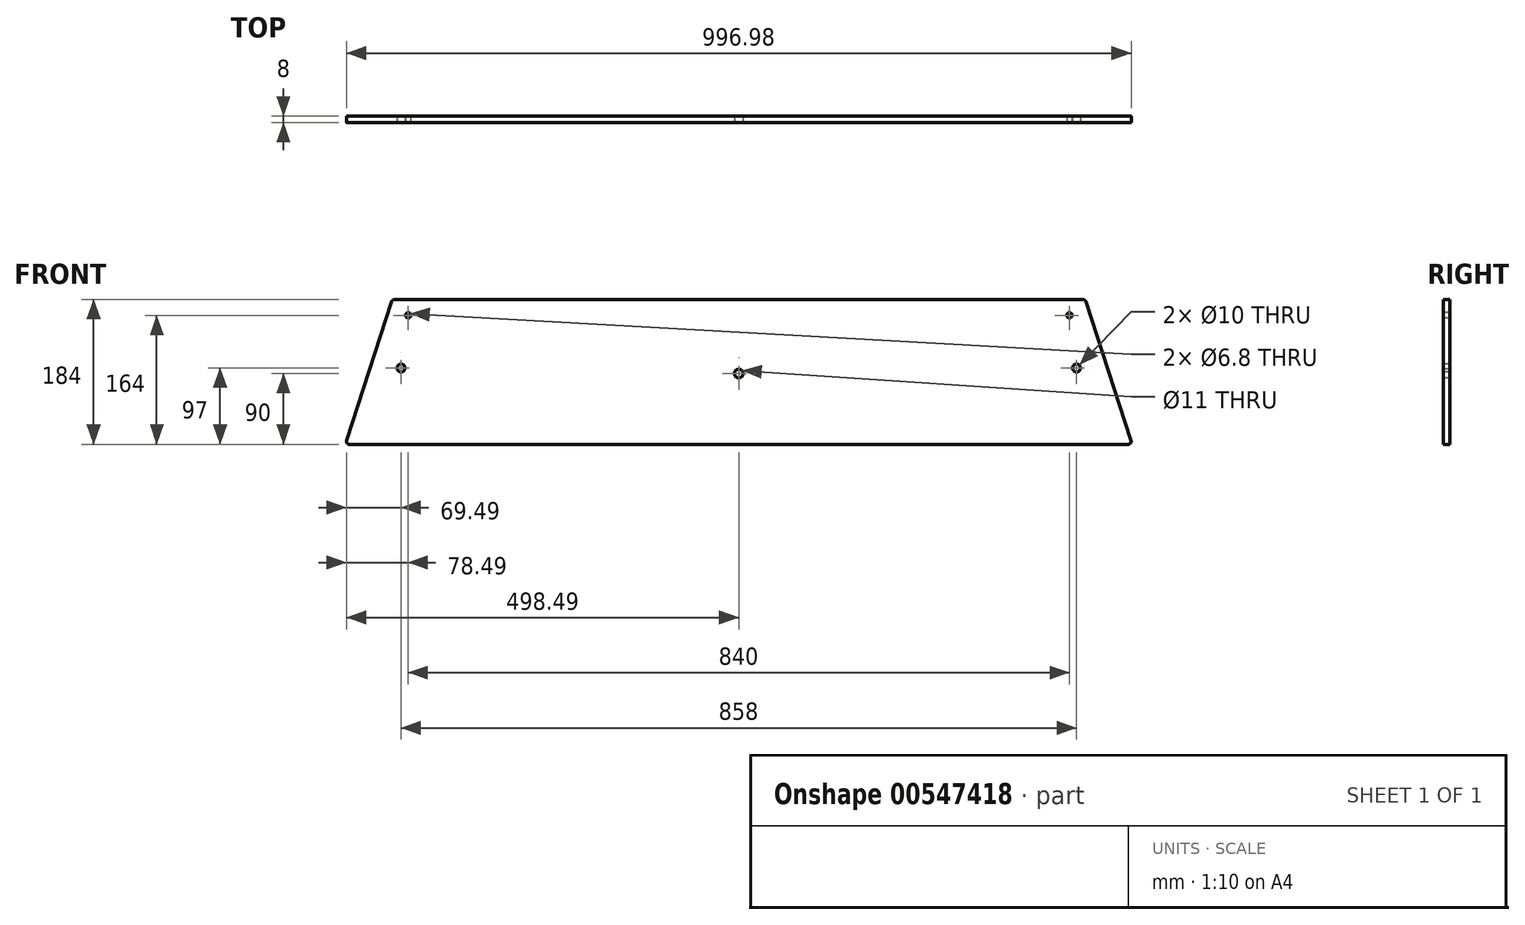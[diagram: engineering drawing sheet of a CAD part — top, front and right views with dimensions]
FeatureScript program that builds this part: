
annotation { "Feature Type Name" : "Feature", "Feature Type Description" : "" }
export const myFeature = defineFeature(function(context is Context, id is Id, definition is map)
    precondition{}
    {
        {
            var Q0;
            Q0=qCreatedBy(makeId("Front.planeOp"),FACE);
            var sketch = newSketch(context, id + "F0", { "sketchPlane" : qUnion([Q0])});
            skLineSegment(sketch, "E0.bottom", {"start": v(440, 92) * mm, "end": v(-440, 92) * mm});
            skLineSegment(sketch, "E0.top", {"start": v(440, -92) * mm, "end": v(-440, -92) * mm});
            skPoint(sketch, "E0.middle", {"position": v(0, 0) * mm});
            skLineSegment(sketch, "E1", {"start": v(440, 92) * mm, "end": v(500, -92) * mm});
            skLineSegment(sketch, "E2", {"start": v(500, -92) * mm, "end": v(440, -92) * mm});
            skLineSegment(sketch, "E3", {"start": v(-440, 92) * mm, "end": v(-500, -92) * mm});
            skLineSegment(sketch, "E4", {"start": v(-500, -92) * mm, "end": v(-440, -92) * mm});
            skSolve(sketch);
        }
        {
            var Q0;
            Q0 = qSketchRegion(id + "F0", true);
            extrude(context, id + "F1", {"entities" : qUnion([Q0]), "endBound" : BoundingType.SYMMETRIC, "depth" : 8 * mm, "offsetDistance" : 25 * mm});
        }
        {
            var Q0;
            Q0=makeQuery(id+"F1.opExtrude","CAP_FACE",FACE,{"disambiguationData":[OSD([sQuery(id+"F0.wireOp",EDGE,"E0.bottom"),sQuery(id+"F0.wireOp",EDGE,"E0.top"),sQuery(id+"F0.wireOp",EDGE,"E0.left"),sQuery(id+"F0.wireOp",EDGE,"E0.right")])],"isStart":false});
            var sketch = newSketch(context, id + "F2", { "sketchPlane" : qUnion([Q0])});
            skCircle(sketch, "E5", {"center": v(429, 5) * mm, "radius": 5 * mm});
            skCircle(sketch, "E6", {"center": v(420, 72) * mm, "radius": 3.4 * mm});
            skCircle(sketch, "E7", {"center": v(-420, 72) * mm, "radius": 3.4 * mm});
            skCircle(sketch, "E8", {"center": v(-429, 5) * mm, "radius": 5 * mm});
            skCircle(sketch, "E9", {"center": v(0, -2) * mm, "radius": 5.5 * mm});
            skLineSegment(sketch, "E10", {"start": v(-34.9, 92) * mm, "end": v(45.26, 92) * mm});
            skSolve(sketch);
        }
        {
            var Q0;
            Q0 = qSketchRegion(id + "F2", true);
            extrude(context, id + "F3", {"entities" : qUnion([Q0]), "operationType" : NewBodyOperationType.REMOVE, "oppositeDirection" : true, "depth" : 8 * mm, "offsetDistance" : 25 * mm});
        }
        {
            var Q0;
            Q0=makeQuery(id+"F1.opExtrude","SWEPT_EDGE",EDGE,{"disambiguationData":[OSD([sQuery(id+"F0.wireOp",EDGE,"E1"),sQuery(id+"F0.wireOp",EDGE,"E2")])]});
            var Q1;
            Q1=makeQuery(id+"F1.opExtrude","SWEPT_EDGE",EDGE,{"disambiguationData":[OSD([sQuery(id+"F0.wireOp",EDGE,"E3"),sQuery(id+"F0.wireOp",EDGE,"E4")])]});
            var Q2;
            Q2=makeQuery(id+"F1.opExtrude","SWEPT_EDGE",EDGE,{"disambiguationData":[OSD([sQuery(id+"F0.wireOp",EDGE,"E0.bottom"),sQuery(id+"F0.wireOp",EDGE,"E1")])]});
            var Q3;
            Q3=makeQuery(id+"F1.opExtrude","SWEPT_EDGE",EDGE,{"disambiguationData":[OSD([sQuery(id+"F0.wireOp",EDGE,"E0.bottom"),sQuery(id+"F0.wireOp",EDGE,"E3")])]});
            fillet(context, id + "F4", {"entities" : qUnion([Q0, Q1, Q2, Q3]), "radius" : 4 * mm, "tangentPropagation" : true, "allowEdgeOverflow" : false});
        }
    });
